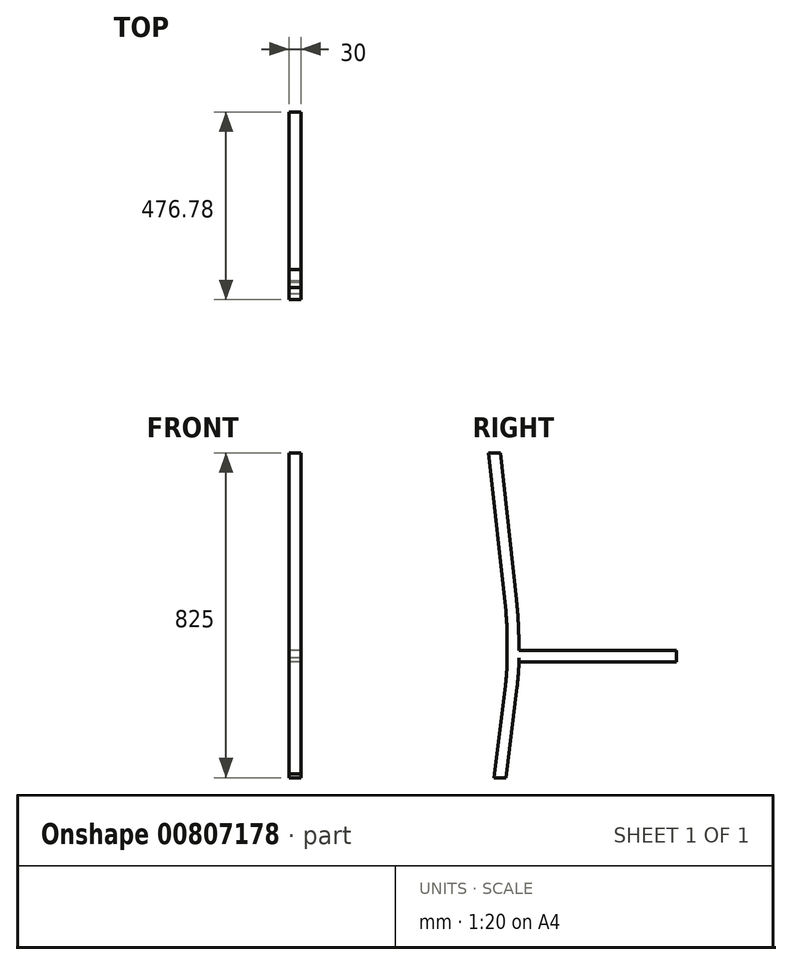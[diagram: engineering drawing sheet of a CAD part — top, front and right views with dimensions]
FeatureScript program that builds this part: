
annotation { "Feature Type Name" : "Feature", "Feature Type Description" : "" }
export const myFeature = defineFeature(function(context is Context, id is Id, definition is map)
    precondition{}
    {
        {
            var Q0;
            Q0=qCreatedBy(makeId("Right.planeOp"),FACE);
            var sketch = newSketch(context, id + "F0", { "sketchPlane" : qUnion([Q0])});
            skLineSegment(sketch, "E0", {"start": v(0, 0) * mm, "end": v(30, 0) * mm});
            skLineSegment(sketch, "E1", {"start": v(30, 0) * mm, "end": v(58.77, 230.33) * mm});
            skLineSegment(sketch, "E2", {"start": v(63.4, 304.7) * mm, "end": v(63.4, 375) * mm});
            skPoint(sketch, "E3.visualSharp", {"position": v(63.4, 267.37) * mm});
            skArc(sketch, "E3.filletArc", {"start": v(58.77, 230.33) * mm, "mid": v(62.24, 267.44) * mm, "end": v(63.4, 304.7) * mm});
            skLineSegment(sketch, "E4.0", {"start": v(33.4, 304.7) * mm, "end": v(33.4, 358.87) * mm});
            skArc(sketch, "E4.1", {"start": v(29, 234.05) * mm, "mid": v(32.3, 269.3) * mm, "end": v(33.4, 304.7) * mm});
            skLineSegment(sketch, "E4.2", {"start": v(0.94, 9.37) * mm, "end": v(29, 234.05) * mm});
            skLineSegment(sketch, "E5", {"start": v(0.94, 9.37) * mm, "end": v(0, 0) * mm});
            skLineSegment(sketch, "E6", {"start": v(29.95, 423.19) * mm, "end": v(-13.38, 825) * mm});
            skPoint(sketch, "E7.visualSharp", {"position": v(33.4, 391.12) * mm});
            skArc(sketch, "E7.filletArc", {"start": v(33.4, 358.87) * mm, "mid": v(32.54, 391.07) * mm, "end": v(29.95, 423.19) * mm});
            skLineSegment(sketch, "E8", {"start": v(-13.38, 825) * mm, "end": v(16.62, 825) * mm});
            skLineSegment(sketch, "E9.0", {"start": v(59.77, 426.43) * mm, "end": v(16.8, 825) * mm});
            skLineSegment(sketch, "E10", {"start": v(16.62, 825) * mm, "end": v(16.8, 825) * mm});
            skLineSegment(sketch, "E11", {"start": v(59.77, 426.43) * mm, "end": v(63.4, 375) * mm});
            skSolve(sketch);
        }
        {
            var Q0;
            Q0 = qSketchRegion(id + "F0", true);
            extrude(context, id + "F1", {"entities" : qUnion([Q0]), "depth" : 30 * mm, "offsetDistance" : 25 * mm});
        }
        {
            var Q0;
            Q0=makeQuery(id+"F1.opExtrude","SWEPT_EDGE",EDGE,{"disambiguationData":[OSD([sQuery(id+"F0.wireOp",EDGE,"E9.0"),sQuery(id+"F0.wireOp",EDGE,"E11")])]});
            var Q1;
            Q1=makeQuery(id+"F1.opExtrude","SWEPT_EDGE",EDGE,{"disambiguationData":[OSD([sQuery(id+"F0.wireOp",EDGE,"E2"),sQuery(id+"F0.wireOp",EDGE,"E11")])]});
            var Q2;
            Q2=makeQuery(id+"F1.opExtrude","SWEPT_EDGE",EDGE,{"disambiguationData":[OSD([sQuery(id+"F0.wireOp",EDGE,"E1"),sQuery(id+"F0.wireOp",EDGE,"E3.filletArc")])]});
            var Q3;
            Q3=makeQuery(id+"F1.opExtrude","SWEPT_EDGE",EDGE,{"disambiguationData":[OSD([sQuery(id+"F0.wireOp",EDGE,"E2"),sQuery(id+"F0.wireOp",EDGE,"E3.filletArc")])]});
            fillet(context, id + "F2", {"entities" : qUnion([Q0, Q1, Q2, Q3]), "radius" : 1450 * mm, "tangentPropagation" : true, "allowEdgeOverflow" : false});
        }
        {
            var Q0;
            {var subQ0=sQuery(id+"F0.wireOp",EDGE,"E11");Q0=makeQuery(id+"F2.opFillet","BLEND_EDGE",EDGE,{"blendedFrom":[makeQuery(id+"F1.opExtrude","SWEPT_EDGE",EDGE,{"disambiguationData":[OSD([sQuery(id+"F0.wireOp",EDGE,"E2"),subQ0])]}),makeQuery(id+"F1.opExtrude","SWEPT_EDGE",EDGE,{"disambiguationData":[OSD([sQuery(id+"F0.wireOp",EDGE,"E9.0"),subQ0])]})],"blendedInto":[]});}
            var Q1;
            {var subQ0=sQuery(id+"F0.wireOp",EDGE,"E2");Q1=makeQuery(id+"F2.opFillet","BLEND_EDGE",EDGE,{"blendedFrom":[makeQuery(id+"F1.opExtrude","SWEPT_EDGE",EDGE,{"disambiguationData":[OSD([subQ0,sQuery(id+"F0.wireOp",EDGE,"E11")])]}),makeQuery(id+"F1.opExtrude","SWEPT_FACE",FACE,{"disambiguationData":[OSD([subQ0])]})],"blendedInto":[makeQuery(id+"F1.opExtrude","SWEPT_FACE",FACE,{"disambiguationData":[OSD([subQ0])]})]});}
            var Q2;
            Q2=makeQuery(id+"F1.opExtrude","SWEPT_EDGE",EDGE,{"disambiguationData":[OSD([sQuery(id+"F0.wireOp",EDGE,"E2"),sQuery(id+"F0.wireOp",EDGE,"E3.filletArc")])]});
            var Q3;
            Q3=makeQuery(id+"F1.opExtrude","SWEPT_EDGE",EDGE,{"disambiguationData":[OSD([sQuery(id+"F0.wireOp",EDGE,"E1"),sQuery(id+"F0.wireOp",EDGE,"E3.filletArc")])]});
            fillet(context, id + "F3", {"entities" : qUnion([Q0, Q1, Q2, Q3]), "radius" : 300 * mm, "tangentPropagation" : true, "allowEdgeOverflow" : false});
        }
        {
            var Q0;
            Q0=makeQuery(id+"F1.opExtrude","SWEPT_FACE",FACE,{"disambiguationData":[OSD([sQuery(id+"F0.wireOp",EDGE,"E2")])]});
            var sketch = newSketch(context, id + "F4", { "sketchPlane" : qUnion([Q0])});
            skLineSegment(sketch, "E12.bottom", {"start": v(-30, 323.85) * mm, "end": v(0, 323.85) * mm});
            skLineSegment(sketch, "E12.top", {"start": v(-30, 293.85) * mm, "end": v(0, 293.85) * mm});
            skLineSegment(sketch, "E12.left", {"start": v(-30, 323.85) * mm, "end": v(-30, 293.85) * mm});
            skLineSegment(sketch, "E12.right", {"start": v(0, 323.85) * mm, "end": v(0, 293.85) * mm});
            skSolve(sketch);
        }
        {
            var Q0;
            Q0 = qSketchRegion(id + "F4", true);
            extrude(context, id + "F5", {"entities" : qUnion([Q0]), "operationType" : NewBodyOperationType.ADD, "depth" : 400 * mm, "offsetDistance" : 25 * mm});
        }
    });
